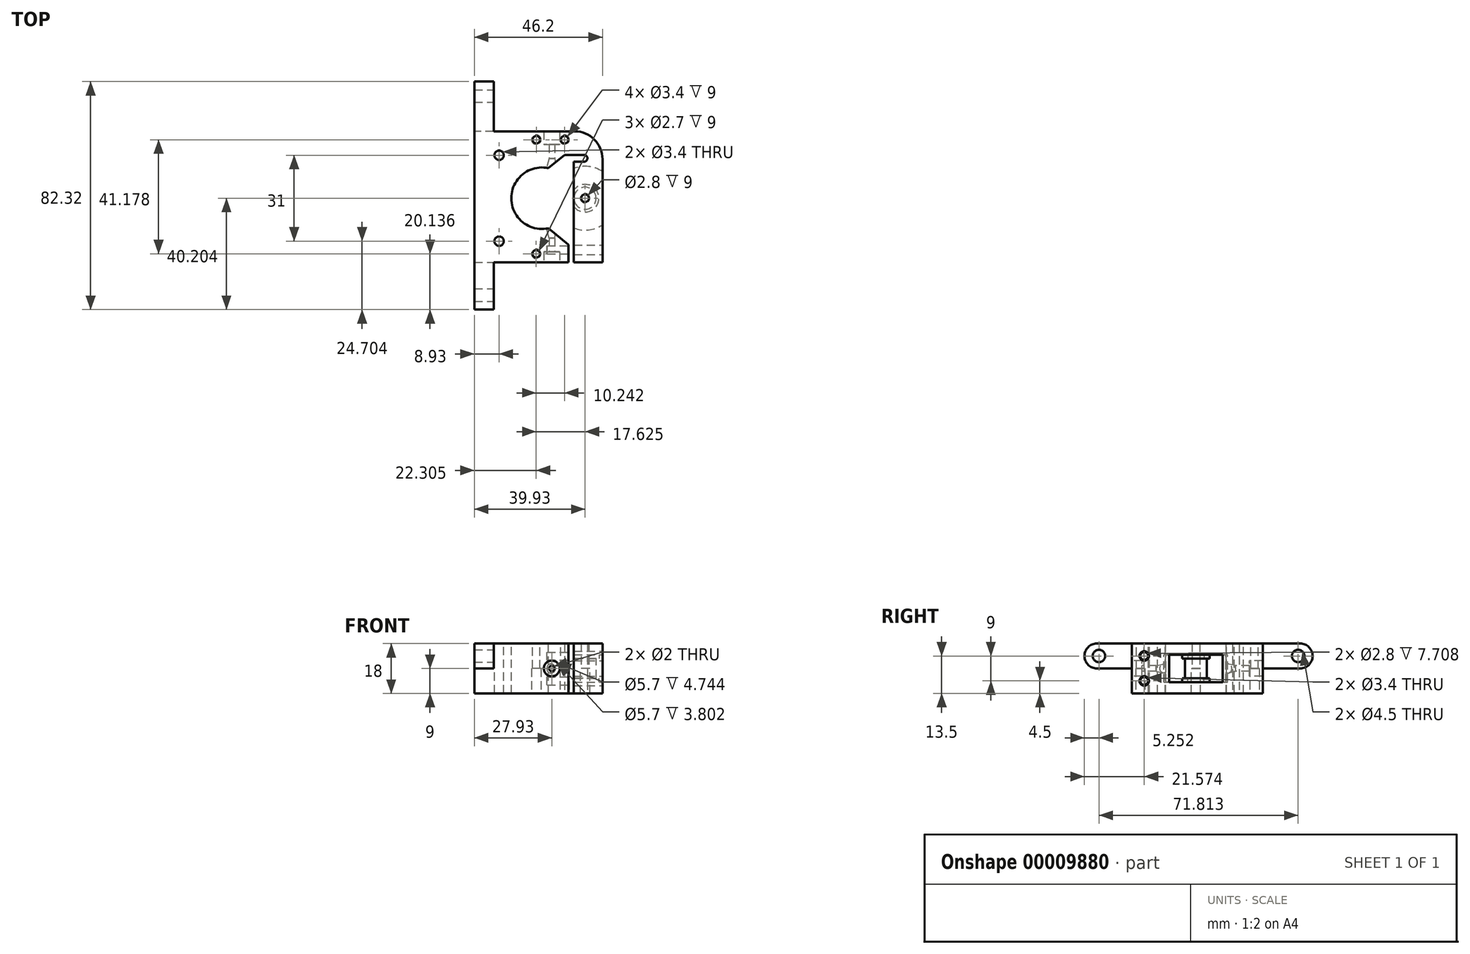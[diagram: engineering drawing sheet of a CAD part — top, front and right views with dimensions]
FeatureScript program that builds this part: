
annotation { "Feature Type Name" : "Feature", "Feature Type Description" : "" }
export const myFeature = defineFeature(function(context is Context, id is Id, definition is map)
    precondition{}
    {
        {
            var Q0;
            Q0=qCreatedBy(makeId("Top.planeOp"),FACE);
            var sketch = newSketch(context, id + "F0", { "sketchPlane" : qUnion([Q0])});
            skLineSegment(sketch, "E0", {"start": v(-24.43, 29.94) * mm, "end": v(-24.43, -17.36) * mm});
            skLineSegment(sketch, "E1", {"start": v(-24.43, -17.36) * mm, "end": v(-24.43, -17.36) * mm});
            skLineSegment(sketch, "E2", {"start": v(-24.43, -17.36) * mm, "end": v(-24.43, -17.35) * mm});
            skLineSegment(sketch, "E3", {"start": v(-24.43, -17.35) * mm, "end": v(9.48, -17.35) * mm});
            skLineSegment(sketch, "E4", {"start": v(9.48, -17.35) * mm, "end": v(9.48, 21.46) * mm});
            skLineSegment(sketch, "E5", {"start": v(9.48, 21.46) * mm, "end": v(15.14, 21.46) * mm});
            skLineSegment(sketch, "E6", {"start": v(15.14, 19) * mm, "end": v(11.48, 19) * mm});
            skLineSegment(sketch, "E7", {"start": v(11.48, 19) * mm, "end": v(11.48, -17.35) * mm});
            skLineSegment(sketch, "E8", {"start": v(11.48, -17.35) * mm, "end": v(21.77, -17.35) * mm});
            skLineSegment(sketch, "E9", {"start": v(21.77, -17.35) * mm, "end": v(21.77, 29.94) * mm});
            skLineSegment(sketch, "E10", {"start": v(21.77, 29.94) * mm, "end": v(-24.43, 29.94) * mm});
            skCircle(sketch, "E11", {"center": v(-2.07, 26.93) * mm, "radius": 1.35 * mm});
            skCircle(sketch, "E12", {"center": v(8.12, 26.93) * mm, "radius": 1.35 * mm});
            skCircle(sketch, "E13", {"center": v(-2.12, -14.24) * mm, "radius": 1.35 * mm});
            skArc(sketch, "E14", {"start": v(15.14, 19) * mm, "mid": v(16.36, 20.23) * mm, "end": v(15.14, 21.46) * mm});
            skCircle(sketch, "E15", {"center": v(-2.07, 26.93) * mm, "radius": 1.7 * mm});
            skCircle(sketch, "E16", {"center": v(8.12, 26.93) * mm, "radius": 1.7 * mm});
            skCircle(sketch, "E17", {"center": v(-2.12, -14.24) * mm, "radius": 1.7 * mm});
            skSolve(sketch);
        }
        {
            var Q0;
            Q0=makeQuery(id+"F0.imprint","IMPRINT",FACE,{"disambiguationData":[TD([[makeQuery(id+"F0.imprint","IMPRINT",EDGE,{"derivedFrom":sQuery(id+"F0.wireOp",EDGE,"E0")}),1.0]])]});
            extrude(context, id + "F1", {"entities" : qUnion([Q0]), "depth" : 9 * mm});
        }
        {
            var Q0;
            Q0=makeQuery(id+"F1.opExtrude","CAP_FACE",FACE,{"disambiguationData":[OSD([sQuery(id+"F0.wireOp",EDGE,"E0"),sQuery(id+"F0.wireOp",EDGE,"E1"),sQuery(id+"F0.wireOp",EDGE,"E2"),sQuery(id+"F0.wireOp",EDGE,"E3"),sQuery(id+"F0.wireOp",EDGE,"E4"),sQuery(id+"F0.wireOp",EDGE,"E5"),sQuery(id+"F0.wireOp",EDGE,"E6"),sQuery(id+"F0.wireOp",EDGE,"E7"),sQuery(id+"F0.wireOp",EDGE,"E8"),sQuery(id+"F0.wireOp",EDGE,"E9"),sQuery(id+"F0.wireOp",EDGE,"E10"),sQuery(id+"F0.wireOp",EDGE,"604cad85-587a-4b7d-8070-06f4cba85480"),sQuery(id+"F0.wireOp",EDGE,"6e5e38c1-5bff-4efe-a8c5-b84022f0a049"),sQuery(id+"F0.wireOp",EDGE,"b8144507-9dd7-4af4-87a3-7b649dd00ae6"),sQuery(id+"F0.wireOp",EDGE,"b9c2cb7c-5e58-4995-888e-a78f0403fbb5"),sQuery(id+"F0.wireOp",EDGE,"885990ab-7576-4c23-8475-595d2769e284"),sQuery(id+"F0.wireOp",EDGE,"E11"),sQuery(id+"F0.wireOp",EDGE,"E12"),sQuery(id+"F0.wireOp",EDGE,"E13"),sQuery(id+"F0.wireOp",EDGE,"E14")])],"isStart":false});
            var sketch = newSketch(context, id + "F2", { "sketchPlane" : qUnion([Q0])});
            skCircle(sketch, "E18", {"center": v(0, 5.82) * mm, "radius": 11.1 * mm});
            skCircle(sketch, "E19", {"center": v(-15.5, 21.32) * mm, "radius": 1.7 * mm});
            skCircle(sketch, "E20", {"center": v(-15.5, -9.68) * mm, "radius": 1.7 * mm});
            skSolve(sketch);
        }
        {
            var Q0;
            Q0 = qSketchRegion(id + "F2", true);
            extrude(context, id + "F3", {"entities" : qUnion([Q0]), "operationType" : NewBodyOperationType.REMOVE, "endBound" : BoundingType.THROUGH_ALL, "oppositeDirection" : true, "depth" : 25 * mm});
        }
        {
            var Q0;
            Q0=makeQuery(id+"F1.opExtrude","CAP_FACE",FACE,{"disambiguationData":[OSD([sQuery(id+"F0.wireOp",EDGE,"E0"),sQuery(id+"F0.wireOp",EDGE,"E1"),sQuery(id+"F0.wireOp",EDGE,"E2"),sQuery(id+"F0.wireOp",EDGE,"E3"),sQuery(id+"F0.wireOp",EDGE,"E4"),sQuery(id+"F0.wireOp",EDGE,"E5"),sQuery(id+"F0.wireOp",EDGE,"E6"),sQuery(id+"F0.wireOp",EDGE,"E7"),sQuery(id+"F0.wireOp",EDGE,"E8"),sQuery(id+"F0.wireOp",EDGE,"E9"),sQuery(id+"F0.wireOp",EDGE,"E10"),sQuery(id+"F0.wireOp",EDGE,"604cad85-587a-4b7d-8070-06f4cba85480"),sQuery(id+"F0.wireOp",EDGE,"6e5e38c1-5bff-4efe-a8c5-b84022f0a049"),sQuery(id+"F0.wireOp",EDGE,"E11"),sQuery(id+"F0.wireOp",EDGE,"E12"),sQuery(id+"F0.wireOp",EDGE,"E13"),sQuery(id+"F0.wireOp",EDGE,"E14")])],"isStart":false});
            var sketch = newSketch(context, id + "F4", { "sketchPlane" : qUnion([Q0])});
            skCircle(sketch, "E21", {"center": v(15.5, 5.82) * mm, "radius": 11.5 * mm});
            skCircle(sketch, "E22", {"center": v(15.5, 5.82) * mm, "radius": 5 * mm});
            skCircle(sketch, "E23", {"center": v(15.5, 5.82) * mm, "radius": 4 * mm});
            skLineSegment(sketch, "E24", {"start": v(0, 5.82) * mm, "end": v(31, 5.82) * mm, "construction": true});
            skCircle(sketch, "E25", {"center": v(15.5, 5.82) * mm, "radius": 1.4 * mm});
            skCircle(sketch, "E26", {"center": v(15.5, 5.82) * mm, "radius": 1.7 * mm});
            skSolve(sketch);
        }
        {
            var Q0;
            Q0=makeQuery(id+"F4.imprint","IMPRINT",FACE,{"disambiguationData":[TD([[makeQuery(id+"F4.imprint","IMPRINT",EDGE,{"derivedFrom":sQuery(id+"F4.wireOp",EDGE,"E22")}),-1.0]])]});
            extrude(context, id + "F5", {"entities" : qUnion([Q0]), "operationType" : NewBodyOperationType.REMOVE, "oppositeDirection" : true, "depth" : 5 * mm});
        }
        {
            var Q0;
            Q0=makeQuery(id+"F4.imprint","IMPRINT",FACE,{"disambiguationData":[TD([[makeQuery(id+"F4.imprint","IMPRINT",EDGE,{"derivedFrom":sQuery(id+"F4.wireOp",EDGE,"E22")}),1.0]])]});
            var Q1;
            Q1=makeQuery(id+"F4.imprint","IMPRINT",FACE,{"disambiguationData":[TD([[makeQuery(id+"F4.imprint","IMPRINT",EDGE,{"derivedFrom":sQuery(id+"F4.wireOp",EDGE,"E23")}),-1.0]])]});
            extrude(context, id + "F6", {"entities" : qUnion([Q0, Q1]), "operationType" : NewBodyOperationType.REMOVE, "oppositeDirection" : true, "depth" : 3.5 * mm});
        }
        {
            var Q0;
            {var subQ0=sQuery(id+"F0.wireOp",EDGE,"E0");var subQ1=sQuery(id+"F0.wireOp",EDGE,"E1");var subQ2=sQuery(id+"F0.wireOp",EDGE,"E2");var subQ3=sQuery(id+"F0.wireOp",EDGE,"E3");var subQ4=sQuery(id+"F0.wireOp",EDGE,"E4");var subQ5=sQuery(id+"F0.wireOp",EDGE,"E5");var subQ6=sQuery(id+"F0.wireOp",EDGE,"E6");var subQ7=sQuery(id+"F0.wireOp",EDGE,"E7");var subQ8=sQuery(id+"F0.wireOp",EDGE,"E9");var subQ9=sQuery(id+"F0.wireOp",EDGE,"E10");var subQ10=sQuery(id+"F0.wireOp",EDGE,"604cad85-587a-4b7d-8070-06f4cba85480");var subQ11=sQuery(id+"F0.wireOp",EDGE,"6e5e38c1-5bff-4efe-a8c5-b84022f0a049");var subQ12=sQuery(id+"F0.wireOp",EDGE,"E11");var subQ13=sQuery(id+"F0.wireOp",EDGE,"E12");var subQ14=sQuery(id+"F0.wireOp",EDGE,"E13");var subQ15=sQuery(id+"F0.wireOp",EDGE,"E14");Q0=makeQuery(id+"F5.boolean.opBoolean","SPLIT",FACE,{"disambiguationData":[TD([makeQuery(id+"F1.opExtrude","SWEPT_FACE",FACE,{"disambiguationData":[OSD([subQ0])]})])],"derivedFrom":makeQuery(id+"F1.opExtrude","CAP_FACE",FACE,{"disambiguationData":[OSD([subQ0,subQ1,subQ2,subQ3,subQ4,subQ5,subQ6,subQ7,sQuery(id+"F0.wireOp",EDGE,"E8"),subQ8,subQ9,subQ10,subQ11,subQ12,subQ13,subQ14,subQ15])],"isStart":false})});}
            var sketch = newSketch(context, id + "F7", { "sketchPlane" : qUnion([Q0])});
            skLineSegment(sketch, "E27", {"start": v(0.65, 30.2) * mm, "end": v(0.65, 25.2) * mm});
            skLineSegment(sketch, "E28", {"start": v(0.65, 25.2) * mm, "end": v(2.5, 25.2) * mm});
            skLineSegment(sketch, "E29", {"start": v(2.5, 25.2) * mm, "end": v(2.5, 20.21) * mm});
            skLineSegment(sketch, "E30", {"start": v(2.5, 20.21) * mm, "end": v(1.31, 15.18) * mm});
            skLineSegment(sketch, "E31", {"start": v(1.31, 15.18) * mm, "end": v(3.5, 15.18) * mm});
            skLineSegment(sketch, "E32", {"start": v(3.5, 15.18) * mm, "end": v(3.5, 30.2) * mm});
            skLineSegment(sketch, "E33", {"start": v(3.5, 30.2) * mm, "end": v(0.65, 30.2) * mm});
            skLineSegment(sketch, "E34", {"start": v(0, 5.82) * mm, "end": v(31.4, 5.82) * mm, "construction": true});
            skLineSegment(sketch, "E35.0.MirrorCS", {"start": v(0.65, -13.54) * mm, "end": v(2.5, -13.54) * mm});
            skLineSegment(sketch, "E35.1.MirrorCS", {"start": v(3.5, -3.53) * mm, "end": v(3.5, -18.54) * mm});
            skLineSegment(sketch, "E35.2.MirrorCS", {"start": v(0.65, -18.54) * mm, "end": v(0.65, -13.54) * mm});
            skLineSegment(sketch, "E35.3.MirrorCS", {"start": v(1.31, -3.53) * mm, "end": v(3.5, -3.53) * mm});
            skLineSegment(sketch, "E35.4.MirrorCS", {"start": v(2.5, -8.56) * mm, "end": v(1.31, -3.53) * mm});
            skLineSegment(sketch, "E35.5.MirrorCS", {"start": v(2.5, -13.54) * mm, "end": v(2.5, -8.56) * mm});
            skLineSegment(sketch, "E35.6.MirrorCS", {"start": v(3.5, -18.54) * mm, "end": v(0.65, -18.54) * mm});
            skSolve(sketch);
        }
        {
            var Q0;
            Q0 = qSketchRegion(id + "F7", true);
            var Q1;
            Q1=sQuery(id+"F7.wireOp",EDGE,"E32");
            revolve(context, id + "F8", {"entities" : qUnion([Q0]), "axis" : qUnion([Q1]), "revolveType" : RevolveType.FULL});
        }
        {
            var Q0;
            Q0=makeQuery(id+"F8.opRevolve","SWEPT_BODY",BODY,{"disambiguationData":[OSD([sQuery(id+"F7.wireOp",EDGE,"E27"),sQuery(id+"F7.wireOp",EDGE,"E28"),sQuery(id+"F7.wireOp",EDGE,"E29"),sQuery(id+"F7.wireOp",EDGE,"E30"),sQuery(id+"F7.wireOp",EDGE,"E31"),sQuery(id+"F7.wireOp",EDGE,"E32"),sQuery(id+"F7.wireOp",EDGE,"E33")])]});
            var Q1;
            Q1=makeQuery(id+"F1.opExtrude","SWEPT_BODY",BODY,{"disambiguationData":[OSD([sQuery(id+"F0.wireOp",EDGE,"E0"),sQuery(id+"F0.wireOp",EDGE,"E1"),sQuery(id+"F0.wireOp",EDGE,"E2"),sQuery(id+"F0.wireOp",EDGE,"E3"),sQuery(id+"F0.wireOp",EDGE,"E4"),sQuery(id+"F0.wireOp",EDGE,"E5"),sQuery(id+"F0.wireOp",EDGE,"E6"),sQuery(id+"F0.wireOp",EDGE,"E7"),sQuery(id+"F0.wireOp",EDGE,"E8"),sQuery(id+"F0.wireOp",EDGE,"E9"),sQuery(id+"F0.wireOp",EDGE,"E10"),sQuery(id+"F0.wireOp",EDGE,"604cad85-587a-4b7d-8070-06f4cba85480"),sQuery(id+"F0.wireOp",EDGE,"6e5e38c1-5bff-4efe-a8c5-b84022f0a049"),sQuery(id+"F0.wireOp",EDGE,"E11"),sQuery(id+"F0.wireOp",EDGE,"E12"),sQuery(id+"F0.wireOp",EDGE,"E13"),sQuery(id+"F0.wireOp",EDGE,"E14")])]});
            booleanBodies(context, id + "F9", {"operationType" : BooleanOperationType.SUBTRACTION, "tools" : qUnion([Q0]), "targets" : qUnion([Q1]), "keepTools" : true});
        }
        {
            var Q0;
            Q0=makeQuery(id+"F8.opRevolve","SWEPT_BODY",BODY,{"disambiguationData":[OSD([sQuery(id+"F7.wireOp",EDGE,"E35.0.MirrorCS"),sQuery(id+"F7.wireOp",EDGE,"E35.1.MirrorCS"),sQuery(id+"F7.wireOp",EDGE,"E35.2.MirrorCS"),sQuery(id+"F7.wireOp",EDGE,"E35.3.MirrorCS"),sQuery(id+"F7.wireOp",EDGE,"E35.4.MirrorCS"),sQuery(id+"F7.wireOp",EDGE,"E35.5.MirrorCS"),sQuery(id+"F7.wireOp",EDGE,"E35.6.MirrorCS")])]});
            var Q1;
            Q1=makeQuery(id+"F1.opExtrude","SWEPT_BODY",BODY,{"disambiguationData":[OSD([sQuery(id+"F0.wireOp",EDGE,"E0"),sQuery(id+"F0.wireOp",EDGE,"E1"),sQuery(id+"F0.wireOp",EDGE,"E2"),sQuery(id+"F0.wireOp",EDGE,"E3"),sQuery(id+"F0.wireOp",EDGE,"E4"),sQuery(id+"F0.wireOp",EDGE,"E5"),sQuery(id+"F0.wireOp",EDGE,"E6"),sQuery(id+"F0.wireOp",EDGE,"E7"),sQuery(id+"F0.wireOp",EDGE,"E8"),sQuery(id+"F0.wireOp",EDGE,"E9"),sQuery(id+"F0.wireOp",EDGE,"E10"),sQuery(id+"F0.wireOp",EDGE,"604cad85-587a-4b7d-8070-06f4cba85480"),sQuery(id+"F0.wireOp",EDGE,"6e5e38c1-5bff-4efe-a8c5-b84022f0a049"),sQuery(id+"F0.wireOp",EDGE,"E11"),sQuery(id+"F0.wireOp",EDGE,"E12"),sQuery(id+"F0.wireOp",EDGE,"E13"),sQuery(id+"F0.wireOp",EDGE,"E14")])]});
            booleanBodies(context, id + "F10", {"operationType" : BooleanOperationType.SUBTRACTION, "tools" : qUnion([Q0]), "targets" : qUnion([Q1]), "keepTools" : true});
        }
        {
            var Q0;
            Q0=makeQuery(id+"F1.opExtrude","SWEPT_EDGE",EDGE,{"disambiguationData":[OSD([sQuery(id+"F0.wireOp",EDGE,"E9"),sQuery(id+"F0.wireOp",EDGE,"E10")])]});
            fillet(context, id + "F11", {"entities" : qUnion([Q0]), "radius" : 10 * mm, "tangentPropagation" : true, "allowEdgeOverflow" : false});
        }
        {
            var Q0;
            Q0 = qSketchRegion(id + "F0", true);
            var Q1;
            Q1=makeQuery(id+"F0.imprint","IMPRINT",FACE,{"disambiguationData":[TD([[makeQuery(id+"F0.imprint","IMPRINT",EDGE,{"derivedFrom":sQuery(id+"F0.wireOp",EDGE,"E12")}),-1.0]])]});
            var Q2;
            Q2=makeQuery(id+"F0.imprint","IMPRINT",FACE,{"disambiguationData":[TD([[makeQuery(id+"F0.imprint","IMPRINT",EDGE,{"derivedFrom":sQuery(id+"F0.wireOp",EDGE,"E11")}),-1.0]])]});
            var Q3;
            Q3=makeQuery(id+"F0.imprint","IMPRINT",FACE,{"disambiguationData":[TD([[makeQuery(id+"F0.imprint","IMPRINT",EDGE,{"derivedFrom":sQuery(id+"F0.wireOp",EDGE,"E13")}),-1.0]])]});
            extrude(context, id + "F12", {"entities" : qUnion([Q0, Q1, Q2, Q3]), "oppositeDirection" : true, "depth" : 9 * mm});
        }
        {
            var Q0;
            Q0=makeQuery(id+"F12.opExtrude","SWEPT_BODY",BODY,{"disambiguationData":[OSD([sQuery(id+"F0.wireOp",EDGE,"E0"),sQuery(id+"F0.wireOp",EDGE,"E3"),sQuery(id+"F0.wireOp",EDGE,"E4"),sQuery(id+"F0.wireOp",EDGE,"E5"),sQuery(id+"F0.wireOp",EDGE,"E6"),sQuery(id+"F0.wireOp",EDGE,"E7"),sQuery(id+"F0.wireOp",EDGE,"E8"),sQuery(id+"F0.wireOp",EDGE,"E9"),sQuery(id+"F0.wireOp",EDGE,"E10"),sQuery(id+"F0.wireOp",EDGE,"E11"),sQuery(id+"F0.wireOp",EDGE,"E12"),sQuery(id+"F0.wireOp",EDGE,"E13"),sQuery(id+"F0.wireOp",EDGE,"E14")])]});
            transform(context, id + "F13", {"entities" : qUnion([Q0]), "transformType" : TransformType.TRANSLATION_3D, "dx" : 0 * mm, "dy" : 0 * mm, "dz" : 18 * mm, "makeCopy" : false});
        }
        {
            var Q0;
            Q0=makeQuery(id+"F12.opExtrude","SWEPT_EDGE",EDGE,{"disambiguationData":[OSD([sQuery(id+"F0.wireOp",EDGE,"E9"),sQuery(id+"F0.wireOp",EDGE,"E10")])]});
            fillet(context, id + "F14", {"entities" : qUnion([Q0]), "radius" : 10 * mm, "tangentPropagation" : true, "allowEdgeOverflow" : false});
        }
        {
            var Q0;
            Q0 = qSketchRegion(id + "F2", true);
            extrude(context, id + "F15", {"entities" : qUnion([Q0]), "operationType" : NewBodyOperationType.REMOVE, "endBound" : BoundingType.THROUGH_ALL, "depth" : 25 * mm});
        }
        {
            var Q0;
            {var subQ3=sQuery(id+"F4.wireOp",EDGE,"E21");var subQ7=makeQuery(id+"F1.opExtrude","CAP_EDGE",EDGE,{"disambiguationData":[OSD([sQuery(id+"F0.wireOp",EDGE,"E9")])],"isStart":false});var subQ9=makeQuery(id+"F4.imprint","INTERSECT",VERTEX,{"disambiguationData":[OD(0.0)],"derivedFrom":[subQ7,subQ3]});Q0=makeQuery(id+"F4.imprint","IMPRINT",FACE,{"disambiguationData":[TD([[makeQuery(id+"F4.imprint","IMPRINT",EDGE,{"disambiguationData":[TD([[subQ9,-1.0]])],"derivedFrom":subQ3}),1.0]])]});}
            extrude(context, id + "F16", {"entities" : qUnion([Q0]), "operationType" : NewBodyOperationType.REMOVE, "depth" : 5 * mm});
        }
        {
            var Q0;
            Q0=makeQuery(id+"F4.imprint","IMPRINT",FACE,{"disambiguationData":[TD([[makeQuery(id+"F4.imprint","IMPRINT",EDGE,{"derivedFrom":sQuery(id+"F4.wireOp",EDGE,"E23")}),-1.0]])]});
            extrude(context, id + "F17", {"entities" : qUnion([Q0]), "operationType" : NewBodyOperationType.REMOVE, "depth" : 3.5 * mm});
        }
        {
            var Q0;
            Q0=makeQuery(id+"F8.opRevolve","SWEPT_BODY",BODY,{"disambiguationData":[OSD([sQuery(id+"F7.wireOp",EDGE,"E27"),sQuery(id+"F7.wireOp",EDGE,"E28"),sQuery(id+"F7.wireOp",EDGE,"E29"),sQuery(id+"F7.wireOp",EDGE,"E30"),sQuery(id+"F7.wireOp",EDGE,"E31"),sQuery(id+"F7.wireOp",EDGE,"E32"),sQuery(id+"F7.wireOp",EDGE,"E33")])]});
            var Q1;
            Q1=makeQuery(id+"F12.opExtrude","SWEPT_BODY",BODY,{"disambiguationData":[OSD([sQuery(id+"F0.wireOp",EDGE,"E0"),sQuery(id+"F0.wireOp",EDGE,"E3"),sQuery(id+"F0.wireOp",EDGE,"E4"),sQuery(id+"F0.wireOp",EDGE,"E5"),sQuery(id+"F0.wireOp",EDGE,"E6"),sQuery(id+"F0.wireOp",EDGE,"E7"),sQuery(id+"F0.wireOp",EDGE,"E8"),sQuery(id+"F0.wireOp",EDGE,"E9"),sQuery(id+"F0.wireOp",EDGE,"E10"),sQuery(id+"F0.wireOp",EDGE,"E11"),sQuery(id+"F0.wireOp",EDGE,"E12"),sQuery(id+"F0.wireOp",EDGE,"E13"),sQuery(id+"F0.wireOp",EDGE,"E14")])]});
            booleanBodies(context, id + "F18", {"operationType" : BooleanOperationType.SUBTRACTION, "tools" : qUnion([Q0]), "targets" : qUnion([Q1])});
        }
        {
            var Q0;
            Q0=makeQuery(id+"F8.opRevolve","SWEPT_BODY",BODY,{"disambiguationData":[OSD([sQuery(id+"F7.wireOp",EDGE,"E35.0.MirrorCS"),sQuery(id+"F7.wireOp",EDGE,"E35.1.MirrorCS"),sQuery(id+"F7.wireOp",EDGE,"E35.2.MirrorCS"),sQuery(id+"F7.wireOp",EDGE,"E35.3.MirrorCS"),sQuery(id+"F7.wireOp",EDGE,"E35.4.MirrorCS"),sQuery(id+"F7.wireOp",EDGE,"E35.5.MirrorCS"),sQuery(id+"F7.wireOp",EDGE,"E35.6.MirrorCS")])]});
            var Q1;
            Q1=makeQuery(id+"F12.opExtrude","SWEPT_BODY",BODY,{"disambiguationData":[OSD([sQuery(id+"F0.wireOp",EDGE,"E0"),sQuery(id+"F0.wireOp",EDGE,"E3"),sQuery(id+"F0.wireOp",EDGE,"E4"),sQuery(id+"F0.wireOp",EDGE,"E5"),sQuery(id+"F0.wireOp",EDGE,"E6"),sQuery(id+"F0.wireOp",EDGE,"E7"),sQuery(id+"F0.wireOp",EDGE,"E8"),sQuery(id+"F0.wireOp",EDGE,"E9"),sQuery(id+"F0.wireOp",EDGE,"E10"),sQuery(id+"F0.wireOp",EDGE,"E11"),sQuery(id+"F0.wireOp",EDGE,"E12"),sQuery(id+"F0.wireOp",EDGE,"E13"),sQuery(id+"F0.wireOp",EDGE,"E14")])]});
            booleanBodies(context, id + "F19", {"operationType" : BooleanOperationType.SUBTRACTION, "tools" : qUnion([Q0]), "targets" : qUnion([Q1])});
        }
        {
            var Q0;
            Q0=makeQuery(id+"F12.opExtrude","SWEPT_FACE",FACE,{"disambiguationData":[OSD([sQuery(id+"F0.wireOp",EDGE,"E9")])]});
            var sketch = newSketch(context, id + "F20", { "sketchPlane" : qUnion([Q0])});
            skCircle(sketch, "E36", {"center": v(-12.8, 13.5) * mm, "radius": 1.7 * mm});
            skCircle(sketch, "E37", {"center": v(-12.8, 13.5) * mm, "radius": 1.4 * mm});
            skCircle(sketch, "E38", {"center": v(-12.8, 4.5) * mm, "radius": 1.7 * mm});
            skCircle(sketch, "E39", {"center": v(-12.8, 4.5) * mm, "radius": 1.4 * mm});
            skSolve(sketch);
        }
        {
            var Q0;
            Q0=makeQuery(id+"F20.imprint","IMPRINT",FACE,{"disambiguationData":[TD([[makeQuery(id+"F20.imprint","IMPRINT",EDGE,{"derivedFrom":sQuery(id+"F20.wireOp",EDGE,"E37")}),1.0]])]});
            extrude(context, id + "F21", {"entities" : qUnion([Q0]), "operationType" : NewBodyOperationType.REMOVE, "oppositeDirection" : true, "depth" : 20 * mm});
        }
        {
            var Q0;
            Q0=makeQuery(id+"F20.imprint","IMPRINT",FACE,{"disambiguationData":[TD([[makeQuery(id+"F20.imprint","IMPRINT",EDGE,{"derivedFrom":sQuery(id+"F20.wireOp",EDGE,"E36")}),1.0]])]});
            extrude(context, id + "F22", {"entities" : qUnion([Q0]), "operationType" : NewBodyOperationType.REMOVE, "oppositeDirection" : true, "depth" : 11 * mm});
        }
        {
            var Q0;
            Q0=makeQuery(id+"F20.imprint","IMPRINT",FACE,{"disambiguationData":[TD([[makeQuery(id+"F20.imprint","IMPRINT",EDGE,{"derivedFrom":sQuery(id+"F20.wireOp",EDGE,"E39")}),1.0]])]});
            extrude(context, id + "F23", {"entities" : qUnion([Q0]), "operationType" : NewBodyOperationType.REMOVE, "oppositeDirection" : true, "depth" : 20 * mm});
        }
        {
            var Q0;
            Q0=makeQuery(id+"F20.imprint","IMPRINT",FACE,{"disambiguationData":[TD([[makeQuery(id+"F20.imprint","IMPRINT",EDGE,{"derivedFrom":sQuery(id+"F20.wireOp",EDGE,"E38")}),1.0]])]});
            extrude(context, id + "F24", {"entities" : qUnion([Q0]), "operationType" : NewBodyOperationType.REMOVE, "oppositeDirection" : true, "depth" : 11 * mm});
        }
        {
            var Q0;
            Q0=makeQuery(id+"F4.imprint","IMPRINT",FACE,{"disambiguationData":[TD([[makeQuery(id+"F4.imprint","IMPRINT",EDGE,{"derivedFrom":sQuery(id+"F4.wireOp",EDGE,"E25")}),1.0]])]});
            var Q1;
            Q1=makeQuery(id+"F4.imprint","IMPRINT",FACE,{"disambiguationData":[TD([[makeQuery(id+"F4.imprint","IMPRINT",EDGE,{"derivedFrom":sQuery(id+"F4.wireOp",EDGE,"E25")}),-1.0]])]});
            extrude(context, id + "F25", {"entities" : qUnion([Q0, Q1]), "operationType" : NewBodyOperationType.REMOVE, "oppositeDirection" : true, "depth" : 25 * mm});
        }
        {
            var Q0;
            Q0=makeQuery(id+"F4.imprint","IMPRINT",FACE,{"disambiguationData":[TD([[makeQuery(id+"F4.imprint","IMPRINT",EDGE,{"derivedFrom":sQuery(id+"F4.wireOp",EDGE,"E25")}),1.0]])]});
            extrude(context, id + "F26", {"entities" : qUnion([Q0]), "operationType" : NewBodyOperationType.REMOVE, "depth" : 25 * mm});
        }
        {
            var Q0;
            Q0=makeQuery(id+"F12.opExtrude","SWEPT_FACE",FACE,{"disambiguationData":[OSD([sQuery(id+"F0.wireOp",EDGE,"E10")])]});
            var sketch = newSketch(context, id + "F27", { "sketchPlane" : qUnion([Q0])});
            skLineSegment(sketch, "E40.bottom", {"start": v(24.43, 9) * mm, "end": v(17.43, 9) * mm});
            skLineSegment(sketch, "E40.top", {"start": v(24.43, 18) * mm, "end": v(17.43, 18) * mm});
            skLineSegment(sketch, "E40.left", {"start": v(24.43, 9) * mm, "end": v(24.43, 18) * mm});
            skLineSegment(sketch, "E40.right", {"start": v(17.43, 9) * mm, "end": v(17.43, 18) * mm});
            skSolve(sketch);
        }
        {
            var Q0;
            Q0 = qSketchRegion(id + "F27", true);
            extrude(context, id + "F28", {"entities" : qUnion([Q0]), "operationType" : NewBodyOperationType.ADD, "depth" : 18 * mm, "hasSecondDirection" : true, "secondDirectionOppositeDirection" : true, "secondDirectionDepth" : 64.31 * mm});
        }
        {
            var Q0;
            {var subQ0=sQuery(id+"F27.wireOp",EDGE,"E40.right");var subQ3=sQuery(id+"F0.wireOp",EDGE,"E3");Q0=makeQuery(id+"F28.boolean.opBoolean","SPLIT",FACE,{"disambiguationData":[TD([makeQuery(id+"F12.opExtrude","SWEPT_FACE",FACE,{"disambiguationData":[OSD([subQ3])]})])],"derivedFrom":makeQuery(id+"F28.opExtrude","SWEPT_FACE",FACE,{"disambiguationData":[OSD([subQ0])]})});}
            var sketch = newSketch(context, id + "F29", { "sketchPlane" : qUnion([Q0])});
            skCircle(sketch, "E41", {"center": v(-29.13, 13.5) * mm, "radius": 2.25 * mm});
            skPoint(sketch, "E42", {"position": v(-34.38, 13.5) * mm});
            skSolve(sketch);
        }
        {
            var Q0;
            {var subQ0=sQuery(id+"F27.wireOp",EDGE,"E40.right");var subQ3=sQuery(id+"F0.wireOp",EDGE,"E10");Q0=makeQuery(id+"F28.boolean.opBoolean","SPLIT",FACE,{"disambiguationData":[TD([makeQuery(id+"F12.opExtrude","SWEPT_FACE",FACE,{"disambiguationData":[OSD([subQ3])]})])],"derivedFrom":makeQuery(id+"F28.opExtrude","SWEPT_FACE",FACE,{"disambiguationData":[OSD([subQ0])]})});}
            var sketch = newSketch(context, id + "F30", { "sketchPlane" : qUnion([Q0])});
            skCircle(sketch, "E43", {"center": v(42.69, 13.5) * mm, "radius": 2.25 * mm});
            skPoint(sketch, "E44", {"position": v(47.94, 13.5) * mm});
            skSolve(sketch);
        }
        {
            var Q0;
            Q0 = qSketchRegion(id + "F29", true);
            var Q1;
            Q1 = qSketchRegion(id + "F30", true);
            extrude(context, id + "F31", {"entities" : qUnion([Q0, Q1]), "operationType" : NewBodyOperationType.REMOVE, "oppositeDirection" : true, "depth" : 25 * mm});
        }
        {
            var Q0;
            Q0=makeQuery(id+"F28.opExtrude","CAP_EDGE",EDGE,{"disambiguationData":[OSD([sQuery(id+"F27.wireOp",EDGE,"E40.top")])],"isStart":true});
            var Q1;
            Q1=makeQuery(id+"F28.opExtrude","CAP_EDGE",EDGE,{"disambiguationData":[OSD([sQuery(id+"F27.wireOp",EDGE,"E40.bottom")])],"isStart":true});
            var Q2;
            Q2=makeQuery(id+"F28.opExtrude","CAP_EDGE",EDGE,{"disambiguationData":[OSD([sQuery(id+"F27.wireOp",EDGE,"E40.top")])],"isStart":false});
            var Q3;
            Q3=makeQuery(id+"F28.opExtrude","CAP_EDGE",EDGE,{"disambiguationData":[OSD([sQuery(id+"F27.wireOp",EDGE,"E40.bottom")])],"isStart":false});
            fillet(context, id + "F32", {"entities" : qUnion([Q0, Q1, Q2, Q3]), "radius" : 4.5 * mm, "tangentPropagation" : true, "allowEdgeOverflow" : false});
        }
        {
            var Q0;
            Q0=makeQuery(id+"F3.boolean.opBoolean","INTERSECT",EDGE,{"disambiguationData":[OD(0.0)],"derivedFrom":[makeQuery(id+"F1.opExtrude","SWEPT_FACE",FACE,{"disambiguationData":[OSD([sQuery(id+"F0.wireOp",EDGE,"E4")])]}),makeQuery(id+"F3.opExtrude","SWEPT_FACE",FACE,{"disambiguationData":[OSD([sQuery(id+"F2.wireOp",EDGE,"E18")])]})]});
            var Q1;
            Q1=makeQuery(id+"F3.boolean.opBoolean","INTERSECT",EDGE,{"disambiguationData":[OD(1.0)],"derivedFrom":[makeQuery(id+"F1.opExtrude","SWEPT_FACE",FACE,{"disambiguationData":[OSD([sQuery(id+"F0.wireOp",EDGE,"E4")])]}),makeQuery(id+"F3.opExtrude","SWEPT_FACE",FACE,{"disambiguationData":[OSD([sQuery(id+"F2.wireOp",EDGE,"E18")])]})]});
            var Q2;
            Q2=makeQuery(id+"F15.boolean.opBoolean","INTERSECT",EDGE,{"disambiguationData":[OD(1.0)],"derivedFrom":[makeQuery(id+"F12.opExtrude","SWEPT_FACE",FACE,{"disambiguationData":[OSD([sQuery(id+"F0.wireOp",EDGE,"E4")])]}),makeQuery(id+"F15.opExtrude","SWEPT_FACE",FACE,{"disambiguationData":[OSD([sQuery(id+"F2.wireOp",EDGE,"E18")])]})]});
            var Q3;
            Q3=makeQuery(id+"F15.boolean.opBoolean","INTERSECT",EDGE,{"disambiguationData":[OD(0.0)],"derivedFrom":[makeQuery(id+"F12.opExtrude","SWEPT_FACE",FACE,{"disambiguationData":[OSD([sQuery(id+"F0.wireOp",EDGE,"E4")])]}),makeQuery(id+"F15.opExtrude","SWEPT_FACE",FACE,{"disambiguationData":[OSD([sQuery(id+"F2.wireOp",EDGE,"E18")])]})]});
            chamfer(context, id + "F33", {"entities" : qUnion([Q0, Q1, Q2, Q3]), "width" : 6 * mm, "tangentPropagation" : true});
        }
    });
